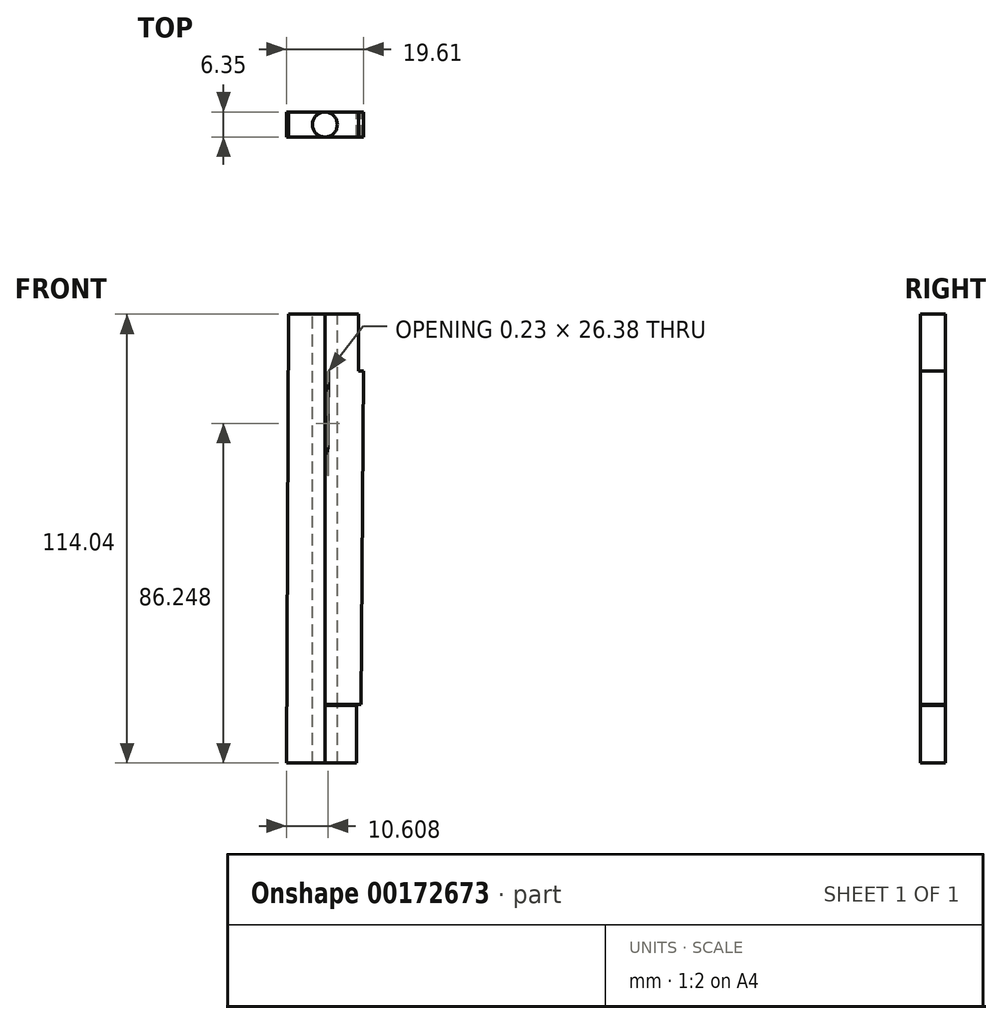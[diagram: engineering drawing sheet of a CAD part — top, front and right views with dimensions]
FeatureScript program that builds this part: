
annotation { "Feature Type Name" : "Feature", "Feature Type Description" : "" }
export const myFeature = defineFeature(function(context is Context, id is Id, definition is map)
    precondition{}
    {
        {
            var Q0;
            Q0=qCreatedBy(makeId("Front.planeOp"),FACE);
            var sketch = newSketch(context, id + "F0", { "sketchPlane" : qUnion([Q0])});
            skLineSegment(sketch, "E0.bottom", {"start": v(57.15, -57.15) * mm, "end": v(-57.15, -57.15) * mm});
            skLineSegment(sketch, "E0.top", {"start": v(57.15, 57.15) * mm, "end": v(-57.15, 57.15) * mm});
            skLineSegment(sketch, "E0.left", {"start": v(57.15, -57.15) * mm, "end": v(57.15, 57.15) * mm});
            skLineSegment(sketch, "E0.right", {"start": v(-57.15, -57.15) * mm, "end": v(-57.15, 57.15) * mm});
            skPoint(sketch, "E0.middle", {"position": v(0, 0) * mm});
            skSolve(sketch);
        }
        {
            var Q0;
            Q0=makeQuery(id+"F0.imprint","IMPRINT",FACE,{"disambiguationData":[TD([[makeQuery(id+"F0.imprint","IMPRINT",EDGE,{"derivedFrom":sQuery(id+"F0.wireOp",EDGE,"E0.bottom")}),-1.0]])]});
            var sketch = newSketch(context, id + "F1", { "sketchPlane" : qUnion([Q0])});
            skLineSegment(sketch, "E1", {"start": v(57.36, 57.02) * mm, "end": v(75.14, 57.02) * mm});
            skLineSegment(sketch, "E2", {"start": v(75.14, 57.02) * mm, "end": v(75.14, 42.42) * mm});
            skLineSegment(sketch, "E3", {"start": v(75.14, 42.42) * mm, "end": v(67.52, 42.42) * mm});
            skLineSegment(sketch, "E4", {"start": v(56.87, -57.02) * mm, "end": v(74.65, -57.02) * mm});
            skLineSegment(sketch, "E5", {"start": v(74.65, -57.02) * mm, "end": v(74.65, -42.42) * mm});
            skLineSegment(sketch, "E6", {"start": v(74.65, -42.42) * mm, "end": v(67.03, -42.42) * mm});
            skLineSegment(sketch, "E7", {"start": v(67.52, 42.42) * mm, "end": v(67.03, -42.42) * mm});
            skLineSegment(sketch, "E8", {"start": v(57.36, 57.02) * mm, "end": v(56.87, -57.02) * mm});
            skSolve(sketch);
        }
        {
            var Q0;
            Q0=makeQuery(id+"F0.imprint","IMPRINT",FACE,{"disambiguationData":[TD([[makeQuery(id+"F0.imprint","IMPRINT",EDGE,{"derivedFrom":sQuery(id+"F0.wireOp",EDGE,"E0.bottom")}),-1.0]])]});
            var sketch = newSketch(context, id + "F2", { "sketchPlane" : qUnion([Q0])});
            skLineSegment(sketch, "E9", {"start": v(67.6, 42.63) * mm, "end": v(76.48, 42.63) * mm});
            skLineSegment(sketch, "E10", {"start": v(75.75, -42.2) * mm, "end": v(66.86, -42.2) * mm});
            skLineSegment(sketch, "E11", {"start": v(67.6, 42.63) * mm, "end": v(66.86, -42.2) * mm});
            skLineSegment(sketch, "E12", {"start": v(76.48, 42.63) * mm, "end": v(75.75, -42.2) * mm});
            skSolve(sketch);
        }
        {
            var Q0;
            {var subQ4=sQuery(id+"F1.wireOp",EDGE,"E1");Q0=makeQuery(id+"F1.imprint","IMPRINT",FACE,{"disambiguationData":[TD([[makeQuery(id+"F1.imprint","IMPRINT",EDGE,{"derivedFrom":subQ4}),-1.0]])]});}
            var Q1;
            Q1 = qSketchRegion(id + "F1", true);
            extrude(context, id + "F3", {"entities" : qUnion([Q0, Q1]), "depth" : 6.35 * mm});
        }
        {
            var Q0;
            Q0=makeQuery(id+"F2.imprint","IMPRINT",FACE,{"disambiguationData":[TD([[makeQuery(id+"F2.imprint","IMPRINT",EDGE,{"derivedFrom":sQuery(id+"F2.wireOp",EDGE,"E9")}),-1.0]])]});
            extrude(context, id + "F4", {"entities" : qUnion([Q0]), "operationType" : NewBodyOperationType.ADD, "depth" : 6.35 * mm});
        }
        {
            var Q0;
            Q0=makeQuery(id+"F3.opExtrude","SWEPT_FACE",FACE,{"disambiguationData":[OSD([sQuery(id+"F1.wireOp",EDGE,"E1")])]});
            var sketch = newSketch(context, id + "F5", { "sketchPlane" : qUnion([Q0])});
            skPoint(sketch, "E13", {"position": v(66.63, -3.18) * mm});
            skCircle(sketch, "E14", {"center": v(66.63, -3.18) * mm, "radius": 3.18 * mm});
            skSolve(sketch);
        }
        {
            var Q0;
            {var subQ0=sQuery(id+"F5.wireOp",EDGE,"E14");var subQ1=sQuery(id+"F1.wireOp",EDGE,"E1");var subQ2=makeQuery(id+"F5.imprint","INTERSECT",VERTEX,{"derivedFrom":[makeQuery(id+"F3.opExtrude","CAP_EDGE",EDGE,{"disambiguationData":[OSD([subQ1])],"isStart":true}),subQ0]});Q0=makeQuery(id+"F5.imprint","IMPRINT",FACE,{"disambiguationData":[TD([[makeQuery(id+"F5.imprint","IMPRINT",EDGE,{"disambiguationData":[TD([[subQ2,-1.0]])],"derivedFrom":subQ0}),1.0]])]});}
            extrude(context, id + "F6", {"entities" : qUnion([Q0]), "operationType" : NewBodyOperationType.REMOVE, "endBound" : BoundingType.THROUGH_ALL, "oppositeDirection" : true, "depth" : 25.4 * mm});
        }
    });
